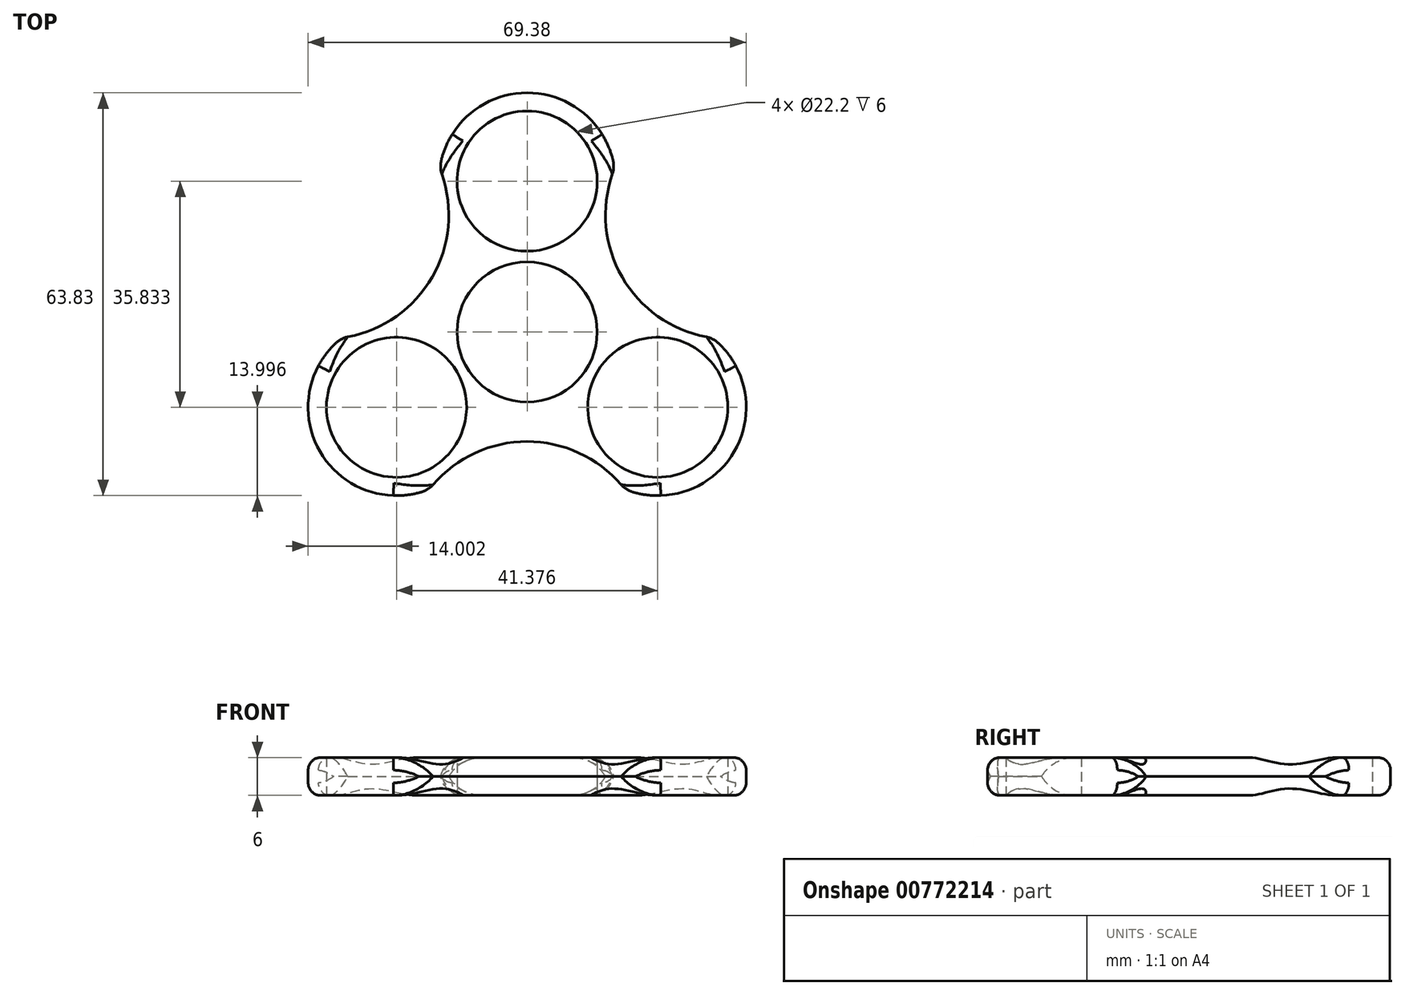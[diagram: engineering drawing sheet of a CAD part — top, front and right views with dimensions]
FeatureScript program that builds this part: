
annotation { "Feature Type Name" : "Feature", "Feature Type Description" : "" }
export const myFeature = defineFeature(function(context is Context, id is Id, definition is map)
    precondition{}
    {
        {
            var Q0;
            Q0=qCreatedBy(makeId("Top.planeOp"),FACE);
            var sketch = newSketch(context, id + "F0", { "sketchPlane" : qUnion([Q0])});
            skCircle(sketch, "E0", {"center": v(0, 0) * mm, "radius": 11.1 * mm});
            skCircle(sketch, "E1", {"center": v(0, 0) * mm, "radius": 3.75 * mm});
            skCircle(sketch, "E2", {"center": v(0, 23.89) * mm, "radius": 11.1 * mm});
            skCircle(sketch, "E3", {"center": v(0, 23.89) * mm, "radius": 3.75 * mm});
            skCircle(sketch, "E4.1.0", {"center": v(-20.69, -11.94) * mm, "radius": 3.75 * mm});
            skCircle(sketch, "E4.1.1", {"center": v(-20.69, -11.94) * mm, "radius": 11.1 * mm});
            skCircle(sketch, "E4.2.0", {"center": v(20.69, -11.94) * mm, "radius": 3.75 * mm});
            skCircle(sketch, "E4.2.1", {"center": v(20.69, -11.94) * mm, "radius": 11.1 * mm});
            skLineSegment(sketch, "E5", {"start": v(-21.01, 24.56) * mm, "end": v(-21.01, 24.56) * mm});
            skArc(sketch, "E6", {"start": v(14, 23.86) * mm, "mid": v(0.01, 37.89) * mm, "end": v(-14, 23.89) * mm});
            skArc(sketch, "E7.1.0", {"start": v(-27.66, 0.2) * mm, "mid": v(-32.82, -18.93) * mm, "end": v(-13.69, -24.07) * mm});
            skArc(sketch, "E7.2.0", {"start": v(13.66, -24.05) * mm, "mid": v(32.8, -18.96) * mm, "end": v(27.69, 0.18) * mm});
            skArc(sketch, "E8", {"start": v(-27.66, 0.2) * mm, "mid": v(-15.73, 9.1) * mm, "end": v(-14, 23.89) * mm});
            skArc(sketch, "E9.1.0", {"start": v(13.66, -24.05) * mm, "mid": v(-0.02, -18.17) * mm, "end": v(-13.69, -24.07) * mm});
            skArc(sketch, "E9.2.0", {"start": v(14, 23.86) * mm, "mid": v(15.75, 9.07) * mm, "end": v(27.69, 0.18) * mm});
            skSolve(sketch);
        }
        {
            var Q0;
            Q0=makeQuery(id+"F0.imprint","IMPRINT",FACE,{"disambiguationData":[TD([[makeQuery(id+"F0.imprint","IMPRINT",EDGE,{"derivedFrom":sQuery(id+"F0.wireOp",EDGE,"E0")}),-1.0]])]});
            extrude(context, id + "F1", {"entities" : qUnion([Q0]), "depth" : 6 * mm, "offsetDistance" : 25 * mm});
        }
        {
            var Q0;
            Q0=makeQuery(id+"F1.opExtrude","CAP_EDGE",EDGE,{"disambiguationData":[OSD([sQuery(id+"F0.wireOp",EDGE,"E9.2.0")])],"isStart":false});
            var Q1;
            Q1=makeQuery(id+"F1.opExtrude","CAP_EDGE",EDGE,{"disambiguationData":[OSD([sQuery(id+"F0.wireOp",EDGE,"E9.2.0")])],"isStart":true});
            var Q2;
            Q2=makeQuery(id+"F1.opExtrude","CAP_EDGE",EDGE,{"disambiguationData":[OSD([sQuery(id+"F0.wireOp",EDGE,"E9.1.0")])],"isStart":false});
            var Q3;
            Q3=makeQuery(id+"F1.opExtrude","CAP_EDGE",EDGE,{"disambiguationData":[OSD([sQuery(id+"F0.wireOp",EDGE,"E9.1.0")])],"isStart":true});
            var Q4;
            Q4=makeQuery(id+"F1.opExtrude","CAP_EDGE",EDGE,{"disambiguationData":[OSD([sQuery(id+"F0.wireOp",EDGE,"E8")])],"isStart":false});
            var Q5;
            Q5=makeQuery(id+"F1.opExtrude","CAP_EDGE",EDGE,{"disambiguationData":[OSD([sQuery(id+"F0.wireOp",EDGE,"E8")])],"isStart":true});
            fillet(context, id + "F2", {"entities" : qUnion([Q0, Q1, Q2, Q3, Q4, Q5]), "radius" : 6 * mm, "tangentPropagation" : true, "allowEdgeOverflow" : false});
        }
        {
            var Q0;
            Q0=makeQuery(id+"F1.opExtrude","CAP_EDGE",EDGE,{"disambiguationData":[OSD([sQuery(id+"F0.wireOp",EDGE,"E6")])],"isStart":true});
            var Q1;
            Q1=makeQuery(id+"F1.opExtrude","CAP_EDGE",EDGE,{"disambiguationData":[OSD([sQuery(id+"F0.wireOp",EDGE,"E6")])],"isStart":false});
            var Q2;
            Q2=makeQuery(id+"F1.opExtrude","CAP_EDGE",EDGE,{"disambiguationData":[OSD([sQuery(id+"F0.wireOp",EDGE,"E7.2.0")])],"isStart":true});
            var Q3;
            Q3=makeQuery(id+"F1.opExtrude","CAP_EDGE",EDGE,{"disambiguationData":[OSD([sQuery(id+"F0.wireOp",EDGE,"E7.2.0")])],"isStart":false});
            var Q4;
            Q4=makeQuery(id+"F1.opExtrude","CAP_EDGE",EDGE,{"disambiguationData":[OSD([sQuery(id+"F0.wireOp",EDGE,"E7.1.0")])],"isStart":true});
            var Q5;
            Q5=makeQuery(id+"F1.opExtrude","CAP_EDGE",EDGE,{"disambiguationData":[OSD([sQuery(id+"F0.wireOp",EDGE,"E7.1.0")])],"isStart":false});
            fillet(context, id + "F3", {"entities" : qUnion([Q0, Q1, Q2, Q3, Q4, Q5]), "radius" : 2 * mm, "tangentPropagation" : true, "allowEdgeOverflow" : false});
        }
    });
